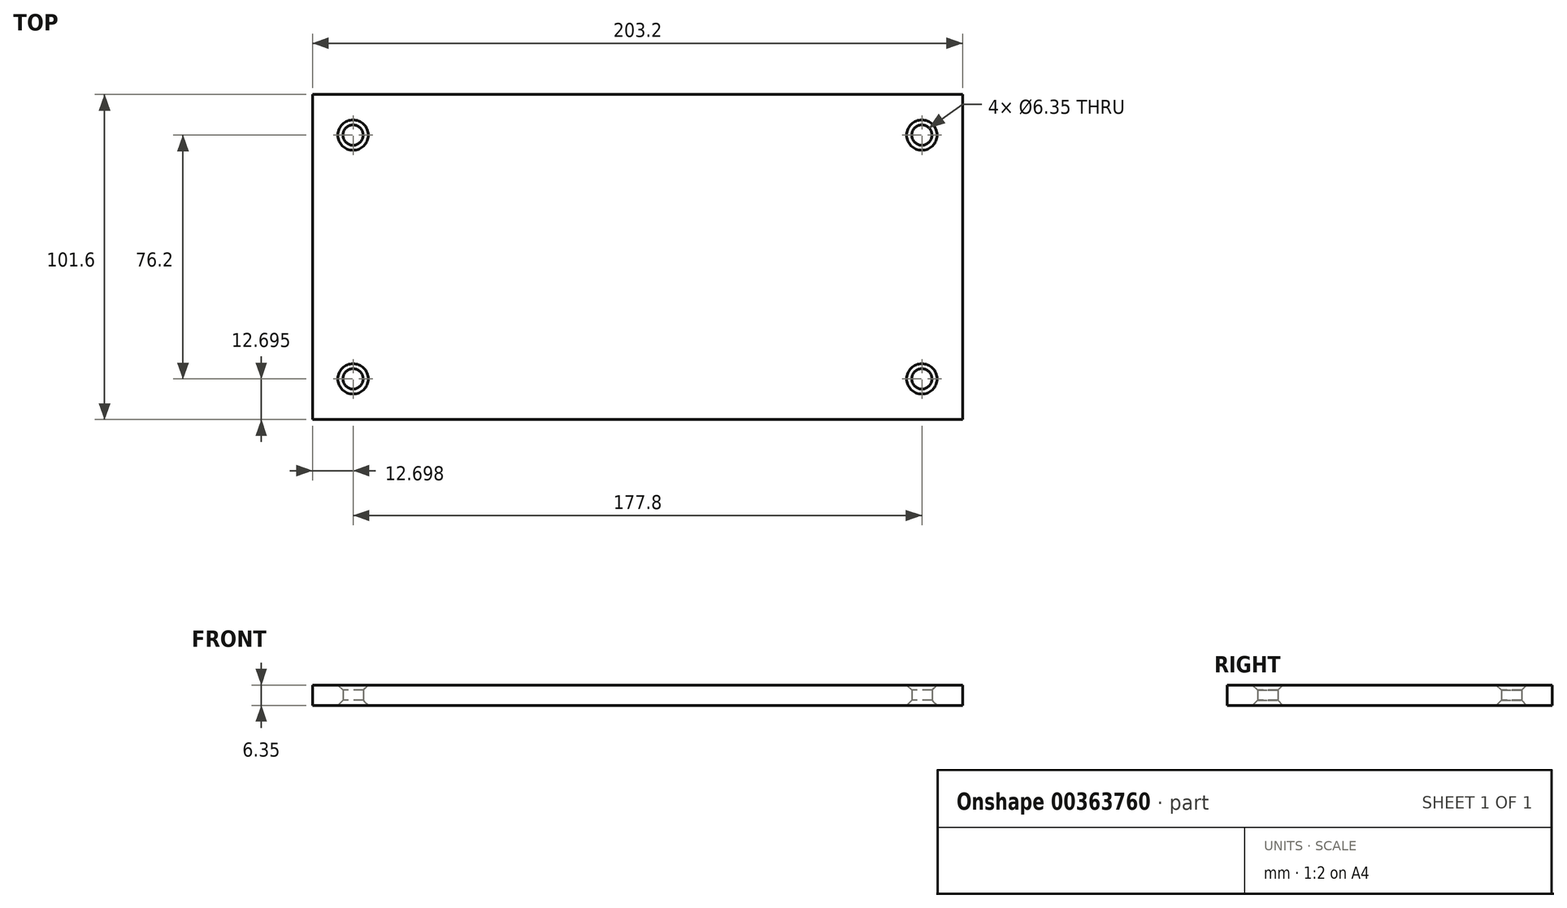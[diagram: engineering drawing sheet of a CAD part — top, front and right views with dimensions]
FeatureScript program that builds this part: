
annotation { "Feature Type Name" : "Feature", "Feature Type Description" : "" }
export const myFeature = defineFeature(function(context is Context, id is Id, definition is map)
    precondition{}
    {
        {
            var Q0;
            Q0=qCreatedBy(makeId("Top.planeOp"),FACE);
            var sketch = newSketch(context, id + "F0", { "sketchPlane" : qUnion([Q0])});
            skLineSegment(sketch, "E0.bottom", {"start": v(-82.81, 67.35) * mm, "end": v(120.39, 67.35) * mm});
            skLineSegment(sketch, "E0.top", {"start": v(-82.81, -34.25) * mm, "end": v(120.39, -34.25) * mm});
            skLineSegment(sketch, "E0.left", {"start": v(-82.81, 67.35) * mm, "end": v(-82.81, -34.25) * mm});
            skLineSegment(sketch, "E0.right", {"start": v(120.39, 67.35) * mm, "end": v(120.39, -34.25) * mm});
            skCircle(sketch, "E1", {"center": v(107.69, 54.65) * mm, "radius": 3.18 * mm});
            skLineSegment(sketch, "E2", {"start": v(18.79, 94) * mm, "end": v(18.79, -48.72) * mm, "construction": true});
            skLineSegment(sketch, "E3", {"start": v(-104.92, 16.55) * mm, "end": v(154.06, 16.55) * mm, "construction": true});
            skCircle(sketch, "E4.MirrorC", {"center": v(-70.11, 54.65) * mm, "radius": 3.18 * mm});
            skCircle(sketch, "E5.MirrorC", {"center": v(-70.11, -21.55) * mm, "radius": 3.18 * mm});
            skCircle(sketch, "E6.MirrorC", {"center": v(107.69, -21.55) * mm, "radius": 3.18 * mm});
            skLineSegment(sketch, "E7", {"start": v(77.54, 92.92) * mm, "end": v(77.54, -72.7) * mm, "construction": true});
            skSolve(sketch);
        }
        {
            var Q0;
            Q0 = qSketchRegion(id + "F0", true);
            extrude(context, id + "F1", {"entities" : qUnion([Q0]), "depth" : 6.35 * mm});
        }
        {
            var Q0;
            Q0=makeQuery(id+"F1.opExtrude","SWEPT_FACE",FACE,{"disambiguationData":[OSD([sQuery(id+"F0.wireOp",EDGE,"E4.MirrorC")])]});
            chamfer(context, id + "F2", {"entities" : qUnion([Q0]), "chamferType" : ChamferType.OFFSET_ANGLE, "width" : 1.57 * mm, "oppositeDirection" : false, "angle" : 45 * degree, "tangentPropagation" : true});
        }
        {
            var Q0;
            Q0=makeQuery(id+"F1.opExtrude","SWEPT_FACE",FACE,{"disambiguationData":[OSD([sQuery(id+"F0.wireOp",EDGE,"E1")])]});
            var Q1;
            Q1=makeQuery(id+"F1.opExtrude","SWEPT_FACE",FACE,{"disambiguationData":[OSD([sQuery(id+"F0.wireOp",EDGE,"E6.MirrorC")])]});
            var Q2;
            Q2=makeQuery(id+"F1.opExtrude","SWEPT_FACE",FACE,{"disambiguationData":[OSD([sQuery(id+"F0.wireOp",EDGE,"E5.MirrorC")])]});
            chamfer(context, id + "F3", {"entities" : qUnion([Q0, Q1, Q2]), "chamferType" : ChamferType.OFFSET_ANGLE, "width" : 1.57 * mm, "oppositeDirection" : false, "angle" : 45 * degree, "tangentPropagation" : true});
        }
    });
